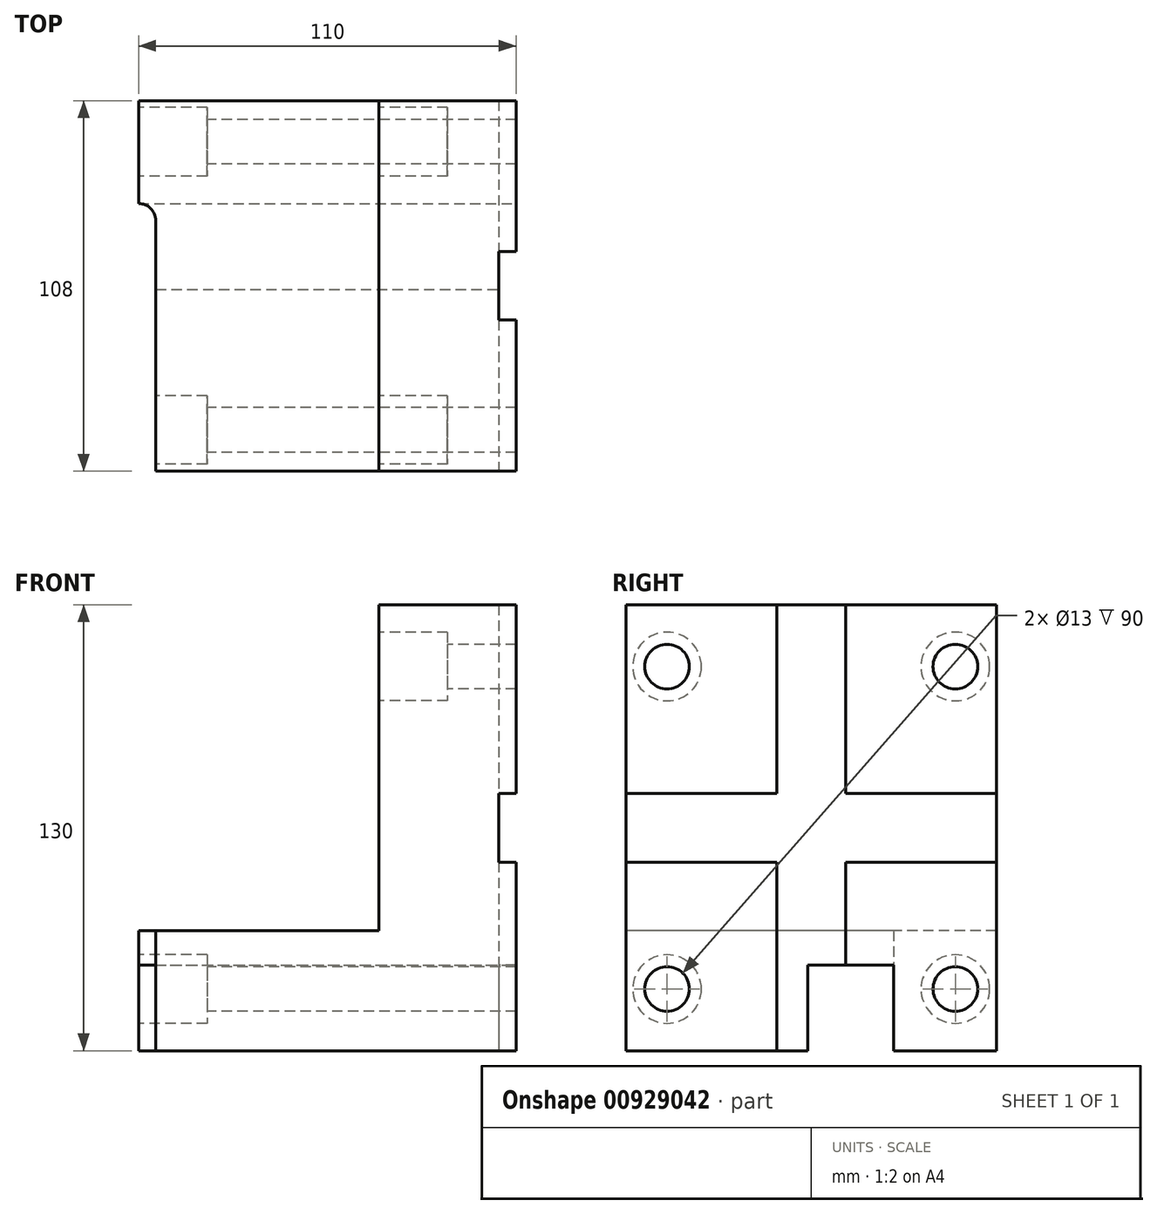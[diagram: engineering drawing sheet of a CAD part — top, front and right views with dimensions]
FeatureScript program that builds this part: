
annotation { "Feature Type Name" : "Feature", "Feature Type Description" : "" }
export const myFeature = defineFeature(function(context is Context, id is Id, definition is map)
    precondition{}
    {
        {
            var Q0;
            Q0=qCreatedBy(makeId("Right.planeOp"),FACE);
            var sketch = newSketch(context, id + "F0", { "sketchPlane" : qUnion([Q0])});
            skLineSegment(sketch, "E0.bottom", {"start": v(54, 65) * mm, "end": v(-54, 65) * mm});
            skLineSegment(sketch, "E0.top", {"start": v(54, -65) * mm, "end": v(-54, -65) * mm});
            skLineSegment(sketch, "E0.left", {"start": v(54, 65) * mm, "end": v(54, -65) * mm});
            skLineSegment(sketch, "E0.right", {"start": v(-54, 65) * mm, "end": v(-54, -65) * mm});
            skPoint(sketch, "E0.middle", {"position": v(0, 0) * mm});
            skSolve(sketch);
        }
        {
            var Q0;
            Q0 = qSketchRegion(id + "F0", true);
            extrude(context, id + "F1", {"entities" : qUnion([Q0]), "oppositeDirection" : true, "depth" : 110 * mm, "offsetDistance" : 25 * mm});
        }
        {
            var Q0;
            Q0=makeQuery(id+"F1.opExtrude","CAP_FACE",FACE,{"disambiguationData":[OSD([sQuery(id+"F0.wireOp",EDGE,"E0.bottom"),sQuery(id+"F0.wireOp",EDGE,"E0.top"),sQuery(id+"F0.wireOp",EDGE,"E0.left"),sQuery(id+"F0.wireOp",EDGE,"E0.right")])],"isStart":false});
            var sketch = newSketch(context, id + "F2", { "sketchPlane" : qUnion([Q0])});
            skCircle(sketch, "E1", {"center": v(-42, 47) * mm, "radius": 6.5 * mm});
            skCircle(sketch, "E2.MirrorC", {"center": v(42, 47) * mm, "radius": 6.5 * mm});
            skCircle(sketch, "E3.MirrorC", {"center": v(-42, -47) * mm, "radius": 6.5 * mm});
            skCircle(sketch, "E4.MirrorC", {"center": v(42, -47) * mm, "radius": 6.5 * mm});
            skSolve(sketch);
        }
        {
            var Q0;
            Q0 = qSketchRegion(id + "F2", true);
            extrude(context, id + "F3", {"entities" : qUnion([Q0]), "operationType" : NewBodyOperationType.REMOVE, "endBound" : BoundingType.THROUGH_ALL, "oppositeDirection" : true, "depth" : 25 * mm, "offsetDistance" : 25 * mm});
        }
        {
            var Q0;
            Q0=makeQuery(id+"F1.opExtrude","CAP_FACE",FACE,{"disambiguationData":[OSD([sQuery(id+"F0.wireOp",EDGE,"E0.bottom"),sQuery(id+"F0.wireOp",EDGE,"E0.top"),sQuery(id+"F0.wireOp",EDGE,"E0.left"),sQuery(id+"F0.wireOp",EDGE,"E0.right")])],"isStart":false});
            var sketch = newSketch(context, id + "F4", { "sketchPlane" : qUnion([Q0])});
            skLineSegment(sketch, "E5.bottom", {"start": v(-54, 65) * mm, "end": v(54, 65) * mm});
            skLineSegment(sketch, "E5.top", {"start": v(-54, -30) * mm, "end": v(54, -30) * mm});
            skLineSegment(sketch, "E5.left", {"start": v(-54, 65) * mm, "end": v(-54, -30) * mm});
            skLineSegment(sketch, "E5.right", {"start": v(54, 65) * mm, "end": v(54, -30) * mm});
            skSolve(sketch);
        }
        {
            var Q0;
            Q0 = qSketchRegion(id + "F4", true);
            extrude(context, id + "F5", {"entities" : qUnion([Q0]), "operationType" : NewBodyOperationType.REMOVE, "oppositeDirection" : true, "depth" : 70 * mm, "offsetDistance" : 25 * mm});
        }
        {
            var Q0;
            Q0=makeQuery(id+"F1.opExtrude","SWEPT_FACE",FACE,{"disambiguationData":[OSD([sQuery(id+"F0.wireOp",EDGE,"E0.top")])]});
            var sketch = newSketch(context, id + "F6", { "sketchPlane" : qUnion([Q0])});
            skLineSegment(sketch, "E6.bottom", {"start": v(-110, -24) * mm, "end": v(0, -24) * mm});
            skLineSegment(sketch, "E6.top", {"start": v(-110, 1) * mm, "end": v(0, 1) * mm});
            skLineSegment(sketch, "E6.left", {"start": v(-110, -24) * mm, "end": v(-110, 1) * mm});
            skLineSegment(sketch, "E6.right", {"start": v(0, -24) * mm, "end": v(0, 1) * mm});
            skSolve(sketch);
        }
        {
            var Q0;
            Q0 = qSketchRegion(id + "F6", true);
            extrude(context, id + "F7", {"entities" : qUnion([Q0]), "operationType" : NewBodyOperationType.REMOVE, "oppositeDirection" : true, "depth" : 25 * mm, "offsetDistance" : 25 * mm});
        }
        {
            var Q0;
            Q0=makeQuery(id+"F1.opExtrude","CAP_FACE",FACE,{"disambiguationData":[OSD([sQuery(id+"F0.wireOp",EDGE,"E0.bottom"),sQuery(id+"F0.wireOp",EDGE,"E0.top"),sQuery(id+"F0.wireOp",EDGE,"E0.left"),sQuery(id+"F0.wireOp",EDGE,"E0.right")])],"isStart":false});
            var sketch = newSketch(context, id + "F8", { "sketchPlane" : qUnion([Q0])});
            skLineSegment(sketch, "E7.0.0", {"start": v(-24, -40) * mm, "end": v(1, -40) * mm});
            skLineSegment(sketch, "E7.0.1", {"start": v(1, -40) * mm, "end": v(1, -65) * mm});
            skLineSegment(sketch, "E7.0.2", {"start": v(1, -65) * mm, "end": v(54, -65) * mm});
            skLineSegment(sketch, "E7.0.3", {"start": v(54, -65) * mm, "end": v(54, -30) * mm});
            skLineSegment(sketch, "E7.0.4", {"start": v(54, -30) * mm, "end": v(-54, -30) * mm});
            skLineSegment(sketch, "E7.0.5", {"start": v(-54, -30) * mm, "end": v(-54, -65) * mm});
            skLineSegment(sketch, "E7.0.6", {"start": v(-54, -65) * mm, "end": v(-24, -65) * mm});
            skLineSegment(sketch, "E7.0.7", {"start": v(-24, -65) * mm, "end": v(-24, -40) * mm});
            skLineSegment(sketch, "E8", {"start": v(-24, -40) * mm, "end": v(-24, -30) * mm});
            skSolve(sketch);
        }
        {
            var Q0;
            Q0=makeQuery(id+"F8.imprint","IMPRINT",FACE,{"disambiguationData":[TD([[makeQuery(id+"F8.imprint","IMPRINT",EDGE,{"derivedFrom":sQuery(id+"F8.wireOp",EDGE,"E7.0.0")}),1.0]])]});
            extrude(context, id + "F9", {"entities" : qUnion([Q0]), "operationType" : NewBodyOperationType.REMOVE, "oppositeDirection" : true, "depth" : 5 * mm, "offsetDistance" : 25 * mm});
        }
        {
            var Q0;
            Q0=makeQuery(id+"F9.boolean.opBoolean","COPY",EDGE,{"derivedFrom":makeQuery(id+"F9.opExtrude","CAP_EDGE",EDGE,{"disambiguationData":[OSD([sQuery(id+"F8.wireOp",EDGE,"E8")])],"isStart":false})});
            fillet(context, id + "F10", {"entities" : qUnion([Q0]), "radius" : 5 * mm, "tangentPropagation" : true, "allowEdgeOverflow" : false});
        }
        {
            var Q0;
            Q0=makeQuery(id+"F5.boolean.opBoolean","COPY",FACE,{"derivedFrom":makeQuery(id+"F5.opExtrude","CAP_FACE",FACE,{"disambiguationData":[OSD([sQuery(id+"F4.wireOp",EDGE,"E5.bottom"),sQuery(id+"F4.wireOp",EDGE,"E5.top"),sQuery(id+"F4.wireOp",EDGE,"E5.left"),sQuery(id+"F4.wireOp",EDGE,"E5.right")])],"isStart":false})});
            var sketch = newSketch(context, id + "F11", { "sketchPlane" : qUnion([Q0])});
            skCircle(sketch, "E9", {"center": v(-42, 47) * mm, "radius": 10 * mm});
            skCircle(sketch, "E10.MirrorC", {"center": v(42, 47) * mm, "radius": 10 * mm});
            skSolve(sketch);
        }
        {
            var Q0;
            Q0 = qSketchRegion(id + "F11", true);
            extrude(context, id + "F12", {"entities" : qUnion([Q0]), "operationType" : NewBodyOperationType.REMOVE, "oppositeDirection" : true, "depth" : 20 * mm, "offsetDistance" : 25 * mm});
        }
        {
            var Q0;
            Q0=makeQuery(id+"F1.opExtrude","CAP_FACE",FACE,{"disambiguationData":[OSD([sQuery(id+"F0.wireOp",EDGE,"E0.bottom"),sQuery(id+"F0.wireOp",EDGE,"E0.top"),sQuery(id+"F0.wireOp",EDGE,"E0.left"),sQuery(id+"F0.wireOp",EDGE,"E0.right")])],"isStart":false});
            var sketch = newSketch(context, id + "F13", { "sketchPlane" : qUnion([Q0])});
            skCircle(sketch, "E11", {"center": v(-42, -47) * mm, "radius": 10 * mm});
            skCircle(sketch, "E12.MirrorC", {"center": v(42, -47) * mm, "radius": 10 * mm});
            skSolve(sketch);
        }
        {
            var Q0;
            Q0 = qSketchRegion(id + "F13", true);
            extrude(context, id + "F14", {"entities" : qUnion([Q0]), "operationType" : NewBodyOperationType.REMOVE, "oppositeDirection" : true, "depth" : 20 * mm, "offsetDistance" : 25 * mm});
        }
        {
            var Q0;
            Q0=makeQuery(id+"F1.opExtrude","CAP_FACE",FACE,{"disambiguationData":[OSD([sQuery(id+"F0.wireOp",EDGE,"E0.bottom"),sQuery(id+"F0.wireOp",EDGE,"E0.top"),sQuery(id+"F0.wireOp",EDGE,"E0.left"),sQuery(id+"F0.wireOp",EDGE,"E0.right")])],"isStart":true});
            var sketch = newSketch(context, id + "F15", { "sketchPlane" : qUnion([Q0])});
            skLineSegment(sketch, "E13.bottom", {"start": v(10, 65) * mm, "end": v(-10, 65) * mm});
            skLineSegment(sketch, "E13.top", {"start": v(10, -65) * mm, "end": v(-10, -65) * mm});
            skLineSegment(sketch, "E13.left", {"start": v(10, 65) * mm, "end": v(10, -65) * mm});
            skLineSegment(sketch, "E13.right", {"start": v(-10, 65) * mm, "end": v(-10, -65) * mm});
            skPoint(sketch, "E13.middle", {"position": v(0, 0) * mm});
            skLineSegment(sketch, "E14.bottom", {"start": v(54, 10) * mm, "end": v(-54, 10) * mm});
            skLineSegment(sketch, "E14.top", {"start": v(54, -10) * mm, "end": v(-54, -10) * mm});
            skLineSegment(sketch, "E14.left", {"start": v(54, 10) * mm, "end": v(54, -10) * mm});
            skLineSegment(sketch, "E14.right", {"start": v(-54, 10) * mm, "end": v(-54, -10) * mm});
            skSolve(sketch);
        }
        {
            var Q0;
            Q0 = qSketchRegion(id + "F15", true);
            extrude(context, id + "F16", {"entities" : qUnion([Q0]), "operationType" : NewBodyOperationType.REMOVE, "oppositeDirection" : true, "depth" : 5 * mm, "offsetDistance" : 25 * mm});
        }
    });
